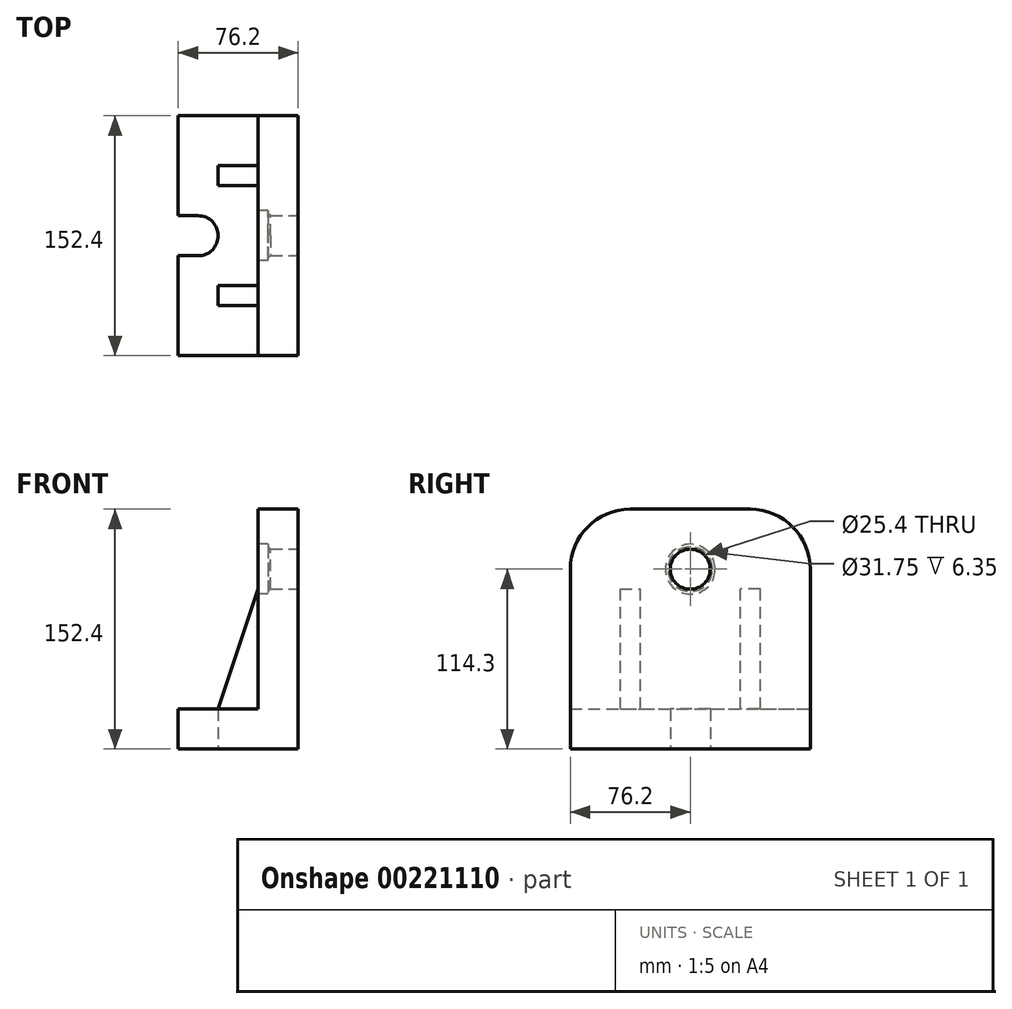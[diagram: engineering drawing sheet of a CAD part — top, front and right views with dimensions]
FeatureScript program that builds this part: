
annotation { "Feature Type Name" : "Feature", "Feature Type Description" : "" }
export const myFeature = defineFeature(function(context is Context, id is Id, definition is map)
    precondition{}
    {
        {
            var Q0;
            Q0=qCreatedBy(makeId("Front.planeOp"),FACE);
            var sketch = newSketch(context, id + "F0", { "sketchPlane" : qUnion([Q0])});
            skLineSegment(sketch, "E0", {"start": v(0, 0) * mm, "end": v(0, 152.4) * mm});
            skLineSegment(sketch, "E1", {"start": v(0, 152.4) * mm, "end": v(-25.4, 152.4) * mm});
            skLineSegment(sketch, "E2", {"start": v(-25.4, 152.4) * mm, "end": v(-25.4, 25.4) * mm});
            skLineSegment(sketch, "E3", {"start": v(-25.4, 25.4) * mm, "end": v(-76.2, 25.4) * mm});
            skLineSegment(sketch, "E4", {"start": v(-76.2, 25.4) * mm, "end": v(-76.2, 0) * mm});
            skLineSegment(sketch, "E5", {"start": v(-76.2, 0) * mm, "end": v(0, 0) * mm});
            skSolve(sketch);
        }
        {
            var Q0;
            Q0=makeQuery(id+"F0.imprint","IMPRINT",FACE,{"disambiguationData":[TD([[makeQuery(id+"F0.imprint","IMPRINT",EDGE,{"derivedFrom":sQuery(id+"F0.wireOp",EDGE,"E0")}),1.0]])]});
            extrude(context, id + "F1", {"entities" : qUnion([Q0]), "endBound" : BoundingType.SYMMETRIC, "depth" : 152.4 * mm});
        }
        {
            var Q0;
            Q0=makeQuery(id+"F1.opExtrude","SWEPT_FACE",FACE,{"disambiguationData":[OSD([sQuery(id+"F0.wireOp",EDGE,"E0")])]});
            var sketch = newSketch(context, id + "F2", { "sketchPlane" : qUnion([Q0])});
            skLineSegment(sketch, "E6", {"start": v(0, 0) * mm, "end": v(0, 152.4) * mm, "construction": true});
            skCircle(sketch, "E7", {"center": v(0, 114.3) * mm, "radius": 12.7 * mm});
            skSolve(sketch);
        }
        {
            var Q0;
            Q0=makeQuery(id+"F2.imprint","IMPRINT",FACE,{"disambiguationData":[TD([[makeQuery(id+"F2.imprint","IMPRINT",EDGE,{"derivedFrom":sQuery(id+"F2.wireOp",EDGE,"E7")}),1.0]])]});
            var Q1;
            Q1=sQuery(id+"F2.wireOp",EDGE,"E7");
            extrude(context, id + "F3", {"entities" : qUnion([Q0]), "operationType" : NewBodyOperationType.REMOVE, "surfaceEntities" : qUnion([Q1]), "endBound" : BoundingType.THROUGH_ALL, "oppositeDirection" : true, "depth" : 25.4 * mm});
        }
        {
            var Q0;
            Q0=makeQuery(id+"F1.opExtrude","SWEPT_FACE",FACE,{"disambiguationData":[OSD([sQuery(id+"F0.wireOp",EDGE,"E5")])]});
            var sketch = newSketch(context, id + "F4", { "sketchPlane" : qUnion([Q0])});
            skLineSegment(sketch, "E8", {"start": v(-76.2, 0) * mm, "end": v(0, 0) * mm, "construction": true});
            skLineSegment(sketch, "E9", {"start": v(-76.2, -12.7) * mm, "end": v(-63.5, -12.7) * mm});
            skLineSegment(sketch, "E10.MirrorCS", {"start": v(-76.2, 12.7) * mm, "end": v(-63.5, 12.7) * mm});
            skArc(sketch, "E11", {"start": v(-63.5, -12.7) * mm, "mid": v(-50.8, 0) * mm, "end": v(-63.5, 12.7) * mm});
            skLineSegment(sketch, "E12", {"start": v(-76.2, -12.7) * mm, "end": v(-76.2, 12.7) * mm});
            skSolve(sketch);
        }
        {
            var Q0;
            Q0 = qSketchRegion(id + "F4", true);
            extrude(context, id + "F5", {"entities" : qUnion([Q0]), "operationType" : NewBodyOperationType.REMOVE, "endBound" : BoundingType.THROUGH_ALL, "oppositeDirection" : true, "depth" : 25.4 * mm});
        }
        {
            var Q0;
            Q0=makeQuery(id+"F1.opExtrude","CAP_EDGE",EDGE,{"disambiguationData":[OSD([sQuery(id+"F0.wireOp",EDGE,"E1")])],"isStart":true});
            var Q1;
            Q1=makeQuery(id+"F1.opExtrude","CAP_EDGE",EDGE,{"disambiguationData":[OSD([sQuery(id+"F0.wireOp",EDGE,"E1")])],"isStart":false});
            fillet(context, id + "F6", {"entities" : qUnion([Q0, Q1]), "radius" : 38.1 * mm, "tangentPropagation" : true, "allowEdgeOverflow" : false});
        }
        {
            var Q0;
            Q0=makeQuery(id+"F1.opExtrude","SWEPT_FACE",FACE,{"disambiguationData":[OSD([sQuery(id+"F0.wireOp",EDGE,"E2")])]});
            var sketch = newSketch(context, id + "F7", { "sketchPlane" : qUnion([Q0])});
            skCircle(sketch, "E13", {"center": v(0, 114.3) * mm, "radius": 15.88 * mm});
            skSolve(sketch);
        }
        {
            var Q0;
            Q0 = qSketchRegion(id + "F7", true);
            extrude(context, id + "F8", {"entities" : qUnion([Q0]), "operationType" : NewBodyOperationType.REMOVE, "oppositeDirection" : true, "depth" : 6.35 * mm});
        }
        {
            var Q0;
            Q0=makeQuery(id+"F1.opExtrude","CAP_FACE",FACE,{"disambiguationData":[OSD([sQuery(id+"F0.wireOp",EDGE,"E0"),sQuery(id+"F0.wireOp",EDGE,"E1"),sQuery(id+"F0.wireOp",EDGE,"E2"),sQuery(id+"F0.wireOp",EDGE,"E3"),sQuery(id+"F0.wireOp",EDGE,"E4"),sQuery(id+"F0.wireOp",EDGE,"E5")])],"isStart":false});
            cPlane(context, id + "F9", {"entities" : qUnion([Q0]), "cplaneType" : CPlaneType.OFFSET, "offset" : 44.45 * mm, "oppositeDirection" : true, "width" : 152.4 * mm, "height" : 152.4 * mm});
        }
        {
            var Q0;
            Q0=qCreatedBy(id+"F9.planeOp",FACE);
            var sketch = newSketch(context, id + "F10", { "sketchPlane" : qUnion([Q0])});
            skLineSegment(sketch, "E14", {"start": v(-50.8, 25.4) * mm, "end": v(-25.4, 25.4) * mm});
            skLineSegment(sketch, "E15", {"start": v(-25.4, 25.4) * mm, "end": v(-25.4, 101.6) * mm});
            skLineSegment(sketch, "E16", {"start": v(-50.8, 25.4) * mm, "end": v(-25.4, 101.6) * mm});
            skSolve(sketch);
        }
        {
            var Q0;
            Q0 = qSketchRegion(id + "F10", true);
            extrude(context, id + "F11", {"entities" : qUnion([Q0]), "operationType" : NewBodyOperationType.ADD, "depth" : 12.7 * mm});
        }
        {
            var Q0;
            Q0=makeQuery(id+"F1.opExtrude","SWEPT_BODY",BODY,{"disambiguationData":[OSD([sQuery(id+"F0.wireOp",EDGE,"E0"),sQuery(id+"F0.wireOp",EDGE,"E1"),sQuery(id+"F0.wireOp",EDGE,"E2"),sQuery(id+"F0.wireOp",EDGE,"E3"),sQuery(id+"F0.wireOp",EDGE,"E4"),sQuery(id+"F0.wireOp",EDGE,"E5")])]});
            var Q1;
            Q1=qCreatedBy(makeId("Front.planeOp"),FACE);
            mirror(context, id + "F12", {"operationType" : NewBodyOperationType.ADD, "entities" : qUnion([Q0]), "mirrorPlane" : qUnion([Q1])});
        }
        {
            var Q0;
            Q0=makeQuery(id+"F8.boolean.opBoolean","COPY",EDGE,{"derivedFrom":makeQuery(id+"F8.opExtrude","CAP_EDGE",EDGE,{"disambiguationData":[OSD([sQuery(id+"F7.wireOp",EDGE,"E13")])],"isStart":true})});
            var Q1;
            Q1=makeQuery(id+"F8.boolean.opBoolean","INTERSECT",EDGE,{"derivedFrom":[makeQuery(id+"F3.boolean.opBoolean","COPY",FACE,{"derivedFrom":makeQuery(id+"F3.opExtrude","SWEPT_FACE",FACE,{"disambiguationData":[OSD([sQuery(id+"F2.wireOp",EDGE,"E7")])]})}),makeQuery(id+"F8.opExtrude","CAP_FACE",FACE,{"disambiguationData":[OSD([sQuery(id+"F7.wireOp",EDGE,"E13")])],"isStart":false})]});
            chamfer(context, id + "F13", {"entities" : qUnion([Q0, Q1]), "width" : 1.52 * mm, "tangentPropagation" : true});
        }
    });
